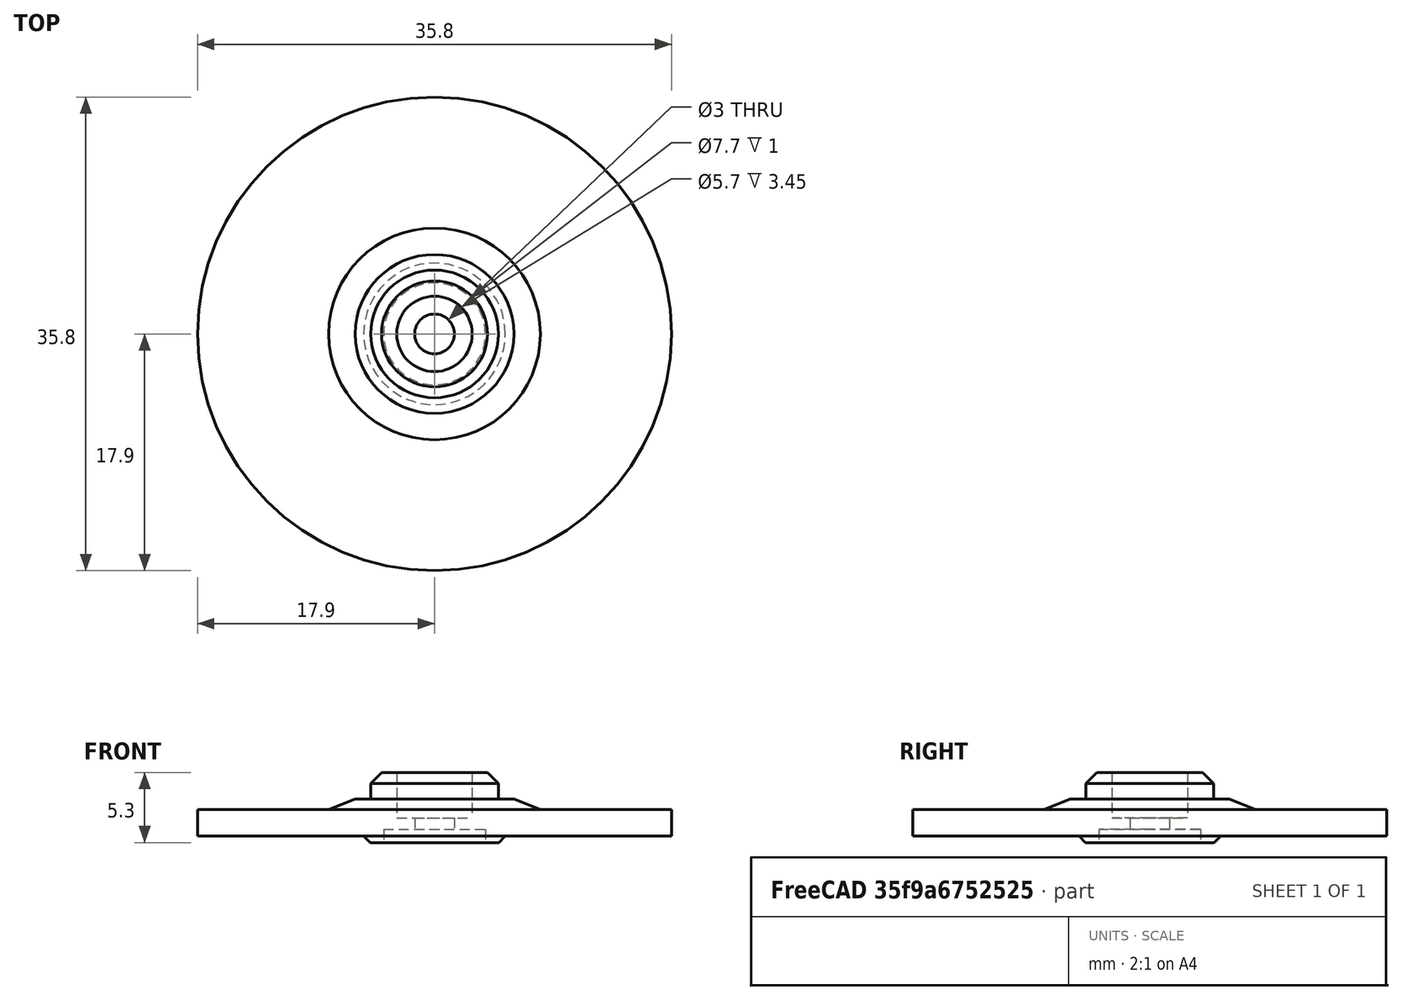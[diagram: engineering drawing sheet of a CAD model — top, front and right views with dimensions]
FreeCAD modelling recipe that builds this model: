
FCSTD DOCUMENT  (FreeCAD 0.18.4R)
Label: large_round_servo_horn
License: All rights reserved
LicenseURL: http://en.wikipedia.org/wiki/All_rights_reserved
objects: Sketcher::SketchObject×1, PartDesign::Revolution×1, PartDesign::Body×1
note: 4 computed .brp shape members not serialized (recipe doc carries the construction recipe); baked Part::Feature solids carry a one-line shape summary decoded from their .brp

FEATURE [Sketcher::SketchObject] Sketch
  MapMode = 5
  Placement = pos=(0,0,0) rot=(1,0,0;1.5708rad)
  Support = -> [XZ_Plane]
  sketch-geometry (15):
    g0: LineSegment StartX=-1.5 StartY=0 StartZ=0 EndX=-1.5 EndY=-0.85 EndZ=0
    g1: LineSegment StartX=-1.5 StartY=-0.85 StartZ=0 EndX=-3.85 EndY=-0.85 EndZ=0
    g2: LineSegment StartX=-3.85 StartY=-0.85 StartZ=0 EndX=-3.85 EndY=-1.85 EndZ=0
    g3: LineSegment StartX=-3.85 StartY=-1.85 StartZ=0 EndX=-4.85 EndY=-1.85 EndZ=0
    g4: LineSegment StartX=-4.85 StartY=-1.85 StartZ=0 EndX=-5.35 EndY=-1.35 EndZ=0
    g5: LineSegment StartX=-5.35 StartY=-1.35 StartZ=0 EndX=-17.9 EndY=-1.35 EndZ=0
    g6: LineSegment StartX=-17.9 StartY=-1.35 StartZ=0 EndX=-17.9 EndY=0.65 EndZ=0
    g7: LineSegment StartX=-17.9 StartY=0.65 StartZ=0 EndX=-8 EndY=0.65 EndZ=0
    g8: LineSegment StartX=-8 StartY=0.65 StartZ=0 EndX=-6 EndY=1.45 EndZ=0
    g9: LineSegment StartX=-6 StartY=1.45 StartZ=0 EndX=-4.825 EndY=1.45 EndZ=0
    g10: LineSegment StartX=-4.825 StartY=1.45 StartZ=0 EndX=-4.825 EndY=2.625 EndZ=0
    g11: LineSegment StartX=-4.825 StartY=2.625 StartZ=0 EndX=-4 EndY=3.45 EndZ=0
    g12: LineSegment StartX=-4 StartY=3.45 StartZ=0 EndX=-2.85 EndY=3.45 EndZ=0
    g13: LineSegment StartX=-2.85 StartY=3.45 StartZ=0 EndX=-2.85 EndY=0 EndZ=0
    g14: LineSegment StartX=-2.85 StartY=0 StartZ=0 EndX=-1.5 EndY=0 EndZ=0
  constraints (45):
    c: Coincident(g0,g1)
    c: Coincident(g1,g2)
    c: Coincident(g2,g3)
    c: Coincident(g3,g4)
    c: Coincident(g4,g5)
    c: Coincident(g5,g6)
    c: Coincident(g6,g7)
    c: Coincident(g7,g8)
    c: Coincident(g8,g9)
    c: Coincident(g9,g10)
    c: Coincident(g10,g11)
    c: Coincident(g11,g12)
    c: Coincident(g12,g13)
    c: Coincident(g13,g14)
    c: Coincident(g14,g0)
    c: Horizontal(g5)
    c: Horizontal(g7)
    c: Horizontal(g9)
    c: Horizontal(g12)
    c: Vertical(g13)
    c: Horizontal(g14)
    c: Vertical(g0)
    c: Horizontal(g1)
    c: Vertical(g2)
    c: Horizontal(g3)
    c: Vertical(g10)
    c: Vertical(g6)
    c: DistanceY(g6,g6) = 2
    c: DistanceX(g6,g-1) = 17.9
    c: DistanceY(g3,g4) = 0.5
    c: DistanceX(g3,g3) = 1
    c: DistanceY(g2,g2) = 1
    c: DistanceX(g4,g3) = 0.5
    c: DistanceX(g1,g-1) = 3.85
    c: DistanceX(g0,g-1) = 1.5
    c: DistanceX(g7,g-1) = 8
    c: DistanceX(g8,g-1) = 6
    c: DistanceY(g7,g8) = 0.8
    c: DistanceX(g10,g-1) = 4.825
    c: DistanceX(g12,g-1) = 2.85
    c: DistanceX(g11,g-1) = 4
    c: DistanceY(g2,g12) = 5.3
    c: DistanceY(g13,g13) = 3.45
    c: Angle(g11,g12) = 2.35619
    c: PointOnObject(g0,g-1)
FEATURE [PartDesign::Revolution] Revolution
  Angle = 360
  Axis = (0,2e-16,1)
  Base = (0,0,0)
  Placement = pos=(0,0,0) rot=(1,0,0;1.5708rad)
  Profile = -> Sketch
  ReferenceAxis = -> Sketch [V_Axis]
FEATURE [PartDesign::Body] Body
  Group = -> [Sketch,Revolution]
  Origin = -> Origin
  Tip = -> Revolution
